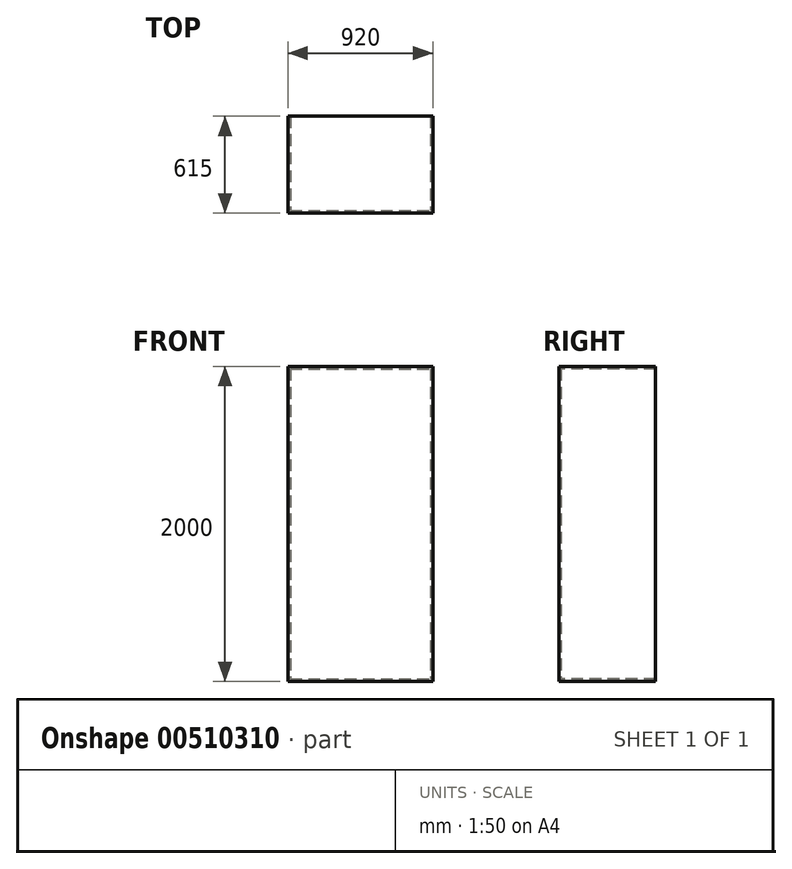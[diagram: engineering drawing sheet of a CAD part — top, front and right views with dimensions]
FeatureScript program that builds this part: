
annotation { "Feature Type Name" : "Feature", "Feature Type Description" : "" }
export const myFeature = defineFeature(function(context is Context, id is Id, definition is map)
    precondition{}
    {
        {
            var Q0;
            Q0=qCreatedBy(makeId("Top.planeOp"),FACE);
            var sketch = newSketch(context, id + "F0", { "sketchPlane" : qUnion([Q0])});
            skLineSegment(sketch, "E0.bottom", {"start": v(-460, 307.5) * mm, "end": v(460, 307.5) * mm});
            skLineSegment(sketch, "E0.top", {"start": v(-460, -307.5) * mm, "end": v(460, -307.5) * mm});
            skLineSegment(sketch, "E0.left", {"start": v(-460, 307.5) * mm, "end": v(-460, -307.5) * mm});
            skLineSegment(sketch, "E0.right", {"start": v(460, 307.5) * mm, "end": v(460, -307.5) * mm});
            skPoint(sketch, "E0.middle", {"position": v(0, 0) * mm});
            skSolve(sketch);
        }
        {
            var Q0;
            Q0=qSketchRegion(id+"F0",true);
            extrude(context, id + "F1", {"entities" : qUnion([Q0]), "depth" : 2000 * mm});
        }
        {
            var Q0;
            Q0=makeQuery(id+"F1.opExtrude","SWEPT_FACE",FACE,{"disambiguationData":[OSD([sQuery(id+"F0.wireOp",EDGE,"E0.bottom")])]});
            shell(context, id + "F2", {"entities" : qUnion([Q0]), "thickness" : 15 * mm});
        }
    });
